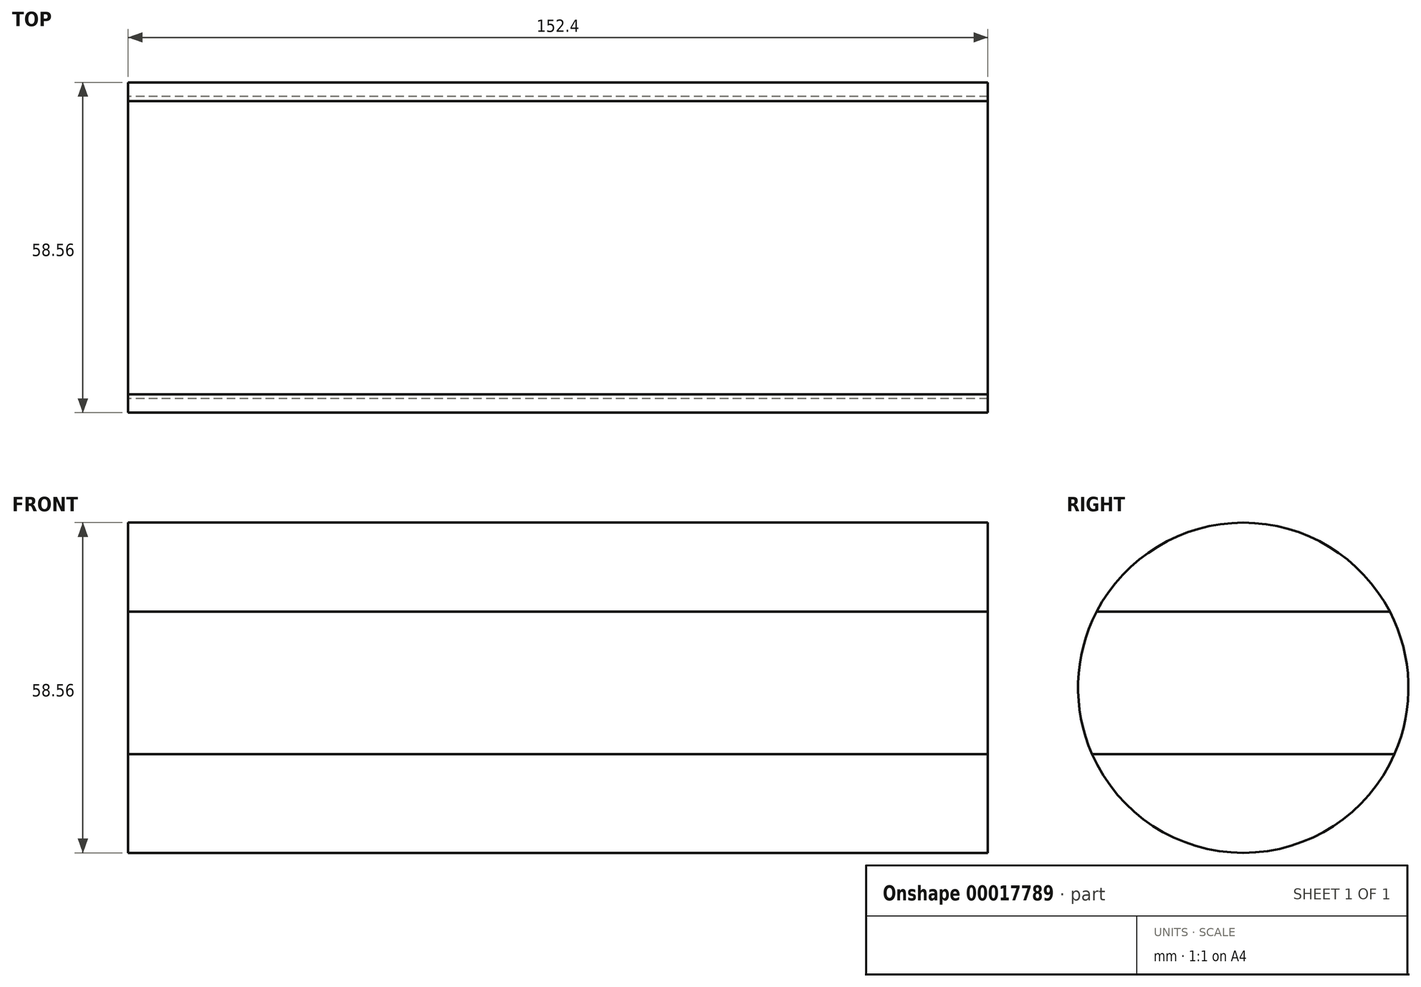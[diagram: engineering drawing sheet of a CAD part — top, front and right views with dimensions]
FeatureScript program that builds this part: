
annotation { "Feature Type Name" : "Feature", "Feature Type Description" : "" }
export const myFeature = defineFeature(function(context is Context, id is Id, definition is map)
    precondition{}
    {
        {
            var Q0;
            Q0=qCreatedBy(makeId("Right.planeOp"),FACE);
            var sketch = newSketch(context, id + "F0", { "sketchPlane" : qUnion([Q0])});
            skCircle(sketch, "E0", {"center": v(0, 0) * mm, "radius": 29.28 * mm});
            skLineSegment(sketch, "E1", {"start": v(-26.81, -11.76) * mm, "end": v(26.81, -11.76) * mm});
            skLineSegment(sketch, "E2", {"start": v(-26, 13.46) * mm, "end": v(26, 13.46) * mm});
            skSolve(sketch);
        }
        {
            var Q0;
            {var subQ0=sQuery(id+"F0.wireOp",EDGE,"E2");Q0=makeQuery(id+"F0.imprint","IMPRINT",FACE,{"disambiguationData":[TD([[makeQuery(id+"F0.imprint","IMPRINT",EDGE,{"derivedFrom":subQ0}),1.0]])]});}
            var Q1;
            {var subQ0=sQuery(id+"F0.wireOp",EDGE,"E1");Q1=makeQuery(id+"F0.imprint","IMPRINT",FACE,{"disambiguationData":[TD([[makeQuery(id+"F0.imprint","IMPRINT",EDGE,{"derivedFrom":subQ0}),-1.0]])]});}
            extrude(context, id + "F1", {"entities" : qUnion([Q0, Q1]), "depth" : 152.4 * mm});
        }
        {
            var Q0;
            {var subQ1=sQuery(id+"F0.wireOp",EDGE,"E1");Q0=makeQuery(id+"F0.imprint","IMPRINT",FACE,{"disambiguationData":[TD([[makeQuery(id+"F0.imprint","IMPRINT",EDGE,{"derivedFrom":subQ1}),1.0]])]});}
            extrude(context, id + "F2", {"entities" : qUnion([Q0]), "depth" : 152.4 * mm});
        }
    });
